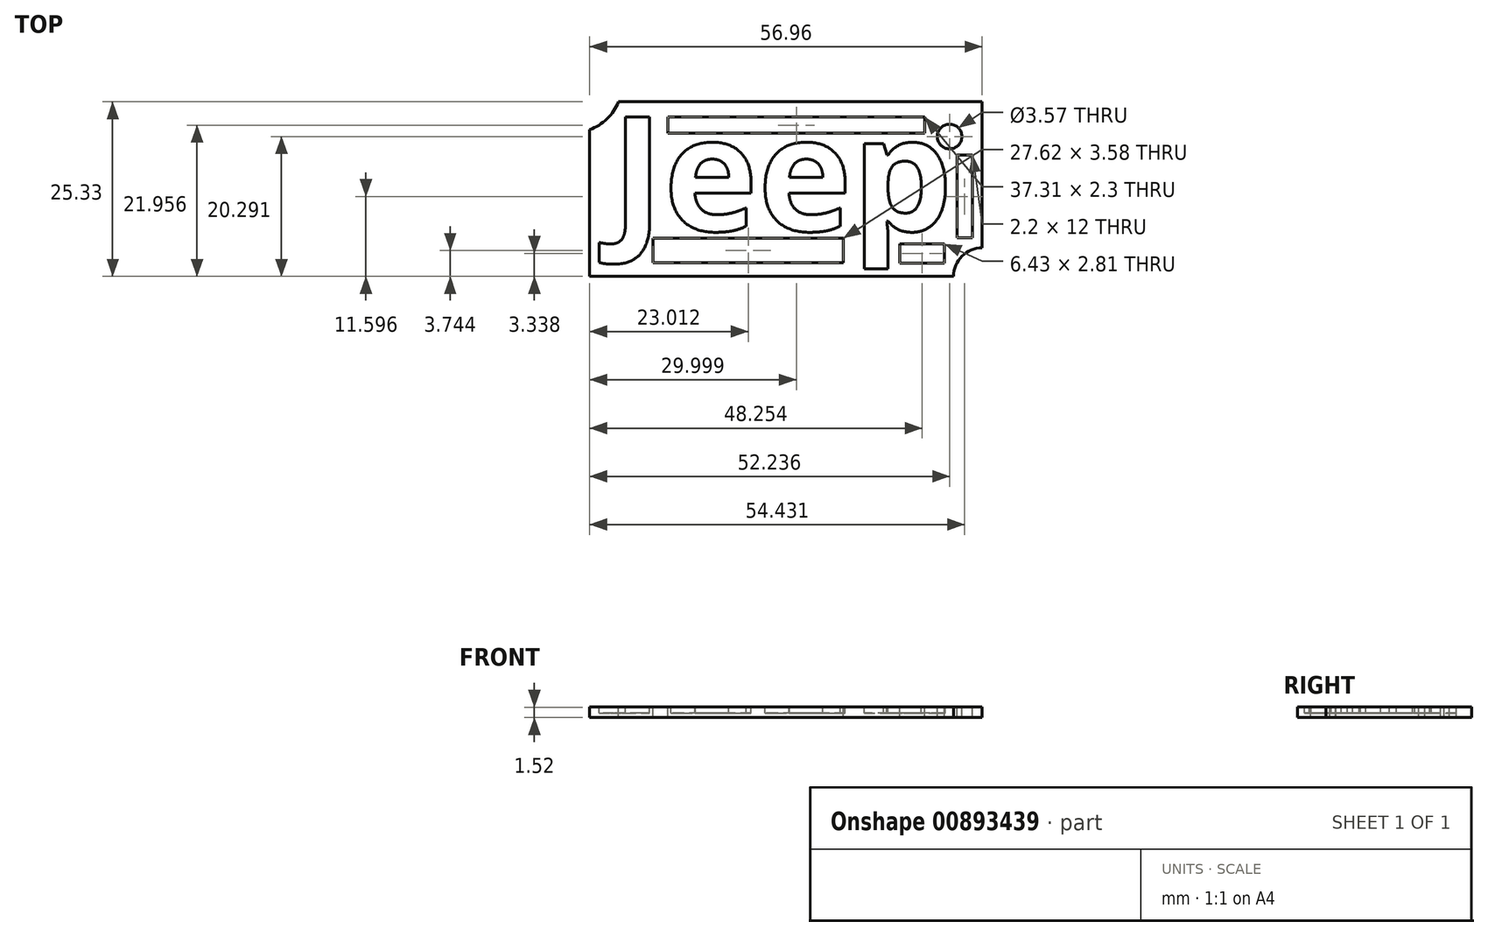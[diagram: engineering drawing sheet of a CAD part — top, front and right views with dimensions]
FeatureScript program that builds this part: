
annotation { "Feature Type Name" : "Feature", "Feature Type Description" : "" }
export const myFeature = defineFeature(function(context is Context, id is Id, definition is map)
    precondition{}
    {
        {
            var Q0;
            Q0=qCreatedBy(makeId("Top.planeOp"),FACE);
            var sketch = newSketch(context, id + "F0", { "sketchPlane" : qUnion([Q0])});
            skLineSegment(sketch, "E0.bottom", {"start": v(-68.58, 25.33) * mm, "end": v(0, 25.33) * mm});
            skLineSegment(sketch, "E0.top", {"start": v(-68.58, 0) * mm, "end": v(0, 0) * mm});
            skLineSegment(sketch, "E0.left", {"start": v(-68.58, 25.33) * mm, "end": v(-68.58, 0) * mm});
            skLineSegment(sketch, "E0.right", {"start": v(0, 25.33) * mm, "end": v(0, 0) * mm});
            skSolve(sketch);
        }
        {
            var Q0;
            Q0 = qSketchRegion(id + "F0", true);
            extrude(context, id + "F1", {"entities" : qUnion([Q0]), "depth" : 1.52 * mm, "offsetDistance" : 25.4 * mm});
        }
        {
            var Q0;
            Q0=makeQuery(id+"F1.opExtrude","CAP_FACE",FACE,{"disambiguationData":[OSD([sQuery(id+"F0.wireOp",EDGE,"E0.bottom"),sQuery(id+"F0.wireOp",EDGE,"E0.top"),sQuery(id+"F0.wireOp",EDGE,"E0.left"),sQuery(id+"F0.wireOp",EDGE,"E0.right")])],"isStart":false});
            var sketch = newSketch(context, id + "F2", { "sketchPlane" : qUnion([Q0])});
            skText(sketch, "E1", { "text": "Jeep", "fontName": "OpenSans-Bold.ttf"});
            const initialGuessF2  = {"E1": [-0.06546, 0.00662, 1, 0, 0.01663]};
            skSetInitialGuess(sketch, initialGuessF2);
            skSolve(sketch);
        }
        {
            var Q0;
            Q0 = qSketchRegion(id + "F2", true);
            extrude(context, id + "F3", {"entities" : qUnion([Q0]), "operationType" : NewBodyOperationType.REMOVE, "oppositeDirection" : true, "depth" : 0.86 * mm, "offsetDistance" : 25.4 * mm});
        }
        {
            var Q0;
            {var subQ0=sQuery(id+"F0.wireOp",EDGE,"E0.left");var subQ1=sQuery(id+"F0.wireOp",EDGE,"E0.bottom");var subQ2=sQuery(id+"F0.wireOp",EDGE,"E0.right");var subQ3=sQuery(id+"F0.wireOp",EDGE,"E0.top");Q0=makeQuery(id+"F3.boolean.opBoolean","SPLIT",FACE,{"disambiguationData":[TD([makeQuery(id+"F1.opExtrude","SWEPT_FACE",FACE,{"disambiguationData":[OSD([subQ1])]})])],"derivedFrom":makeQuery(id+"F1.opExtrude","CAP_FACE",FACE,{"disambiguationData":[OSD([subQ1,subQ3,subQ0,subQ2])],"isStart":false})});}
            var sketch = newSketch(context, id + "F4", { "sketchPlane" : qUnion([Q0])});
            skLineSegment(sketch, "E2.bottom", {"start": v(-11.62, 32.09) * mm, "end": v(9.77, 32.09) * mm});
            skLineSegment(sketch, "E2.top", {"start": v(-11.62, -12.1) * mm, "end": v(9.77, -12.1) * mm});
            skLineSegment(sketch, "E2.left", {"start": v(-11.62, 32.09) * mm, "end": v(-11.62, -12.1) * mm});
            skLineSegment(sketch, "E2.right", {"start": v(9.77, 32.09) * mm, "end": v(9.77, -12.1) * mm});
            skSolve(sketch);
        }
        {
            var Q0;
            Q0 = qSketchRegion(id + "F4", true);
            extrude(context, id + "F5", {"entities" : qUnion([Q0]), "operationType" : NewBodyOperationType.REMOVE, "oppositeDirection" : true, "depth" : 64 * mm, "offsetDistance" : 25.4 * mm});
        }
        {
            var Q0;
            {var subQ0=sQuery(id+"F0.wireOp",EDGE,"E0.left");var subQ1=sQuery(id+"F0.wireOp",EDGE,"E0.bottom");var subQ2=sQuery(id+"F0.wireOp",EDGE,"E0.right");var subQ3=sQuery(id+"F0.wireOp",EDGE,"E0.top");Q0=makeQuery(id+"F3.boolean.opBoolean","SPLIT",FACE,{"disambiguationData":[TD([makeQuery(id+"F1.opExtrude","SWEPT_FACE",FACE,{"disambiguationData":[OSD([subQ1])]})])],"derivedFrom":makeQuery(id+"F1.opExtrude","CAP_FACE",FACE,{"disambiguationData":[OSD([subQ1,subQ3,subQ0,subQ2])],"isStart":false})});}
            var sketch = newSketch(context, id + "F6", { "sketchPlane" : qUnion([Q0])});
            skCircle(sketch, "E3", {"center": v(-16.34, 20.3) * mm, "radius": 1.78 * mm});
            skSolve(sketch);
        }
        {
            var Q0;
            Q0 = qSketchRegion(id + "F6", true);
            extrude(context, id + "F7", {"entities" : qUnion([Q0]), "operationType" : NewBodyOperationType.REMOVE, "oppositeDirection" : true, "depth" : 17.58 * mm, "offsetDistance" : 25.4 * mm});
        }
        {
            var Q0;
            {var subQ0=sQuery(id+"F0.wireOp",EDGE,"E0.left");var subQ1=sQuery(id+"F0.wireOp",EDGE,"E0.bottom");var subQ2=sQuery(id+"F0.wireOp",EDGE,"E0.right");var subQ3=sQuery(id+"F0.wireOp",EDGE,"E0.top");Q0=makeQuery(id+"F3.boolean.opBoolean","SPLIT",FACE,{"disambiguationData":[TD([makeQuery(id+"F1.opExtrude","SWEPT_FACE",FACE,{"disambiguationData":[OSD([subQ1])]})])],"derivedFrom":makeQuery(id+"F1.opExtrude","CAP_FACE",FACE,{"disambiguationData":[OSD([subQ1,subQ3,subQ0,subQ2])],"isStart":false})});}
            var sketch = newSketch(context, id + "F8", { "sketchPlane" : qUnion([Q0])});
            skCircle(sketch, "E4", {"center": v(-71, 28.01) * mm, "radius": 7.14 * mm});
            skSolve(sketch);
        }
        {
            var Q0;
            Q0 = qSketchRegion(id + "F8", true);
            extrude(context, id + "F9", {"entities" : qUnion([Q0]), "operationType" : NewBodyOperationType.REMOVE, "oppositeDirection" : true, "depth" : 58.67 * mm, "offsetDistance" : 25.4 * mm});
        }
        {
            var Q0;
            {var subQ0=sQuery(id+"F0.wireOp",EDGE,"E0.left");var subQ1=sQuery(id+"F0.wireOp",EDGE,"E0.bottom");var subQ2=sQuery(id+"F0.wireOp",EDGE,"E0.right");var subQ3=sQuery(id+"F0.wireOp",EDGE,"E0.top");Q0=makeQuery(id+"F3.boolean.opBoolean","SPLIT",FACE,{"disambiguationData":[TD([makeQuery(id+"F1.opExtrude","SWEPT_FACE",FACE,{"disambiguationData":[OSD([subQ1])]})])],"derivedFrom":makeQuery(id+"F1.opExtrude","CAP_FACE",FACE,{"disambiguationData":[OSD([subQ1,subQ3,subQ0,subQ2])],"isStart":false})});}
            var sketch = newSketch(context, id + "F10", { "sketchPlane" : qUnion([Q0])});
            skCircle(sketch, "E5", {"center": v(-11.62, 0) * mm, "radius": 4.16 * mm});
            skSolve(sketch);
        }
        {
            var Q0;
            Q0 = qSketchRegion(id + "F10", true);
            extrude(context, id + "F11", {"entities" : qUnion([Q0]), "operationType" : NewBodyOperationType.REMOVE, "oppositeDirection" : true, "depth" : 87.88 * mm, "offsetDistance" : 25.4 * mm});
        }
        {
            var Q0;
            {var subQ0=sQuery(id+"F0.wireOp",EDGE,"E0.left");var subQ1=sQuery(id+"F0.wireOp",EDGE,"E0.bottom");var subQ2=sQuery(id+"F0.wireOp",EDGE,"E0.right");var subQ3=sQuery(id+"F0.wireOp",EDGE,"E0.top");Q0=makeQuery(id+"F3.boolean.opBoolean","SPLIT",FACE,{"disambiguationData":[TD([makeQuery(id+"F1.opExtrude","SWEPT_FACE",FACE,{"disambiguationData":[OSD([subQ1])]})])],"derivedFrom":makeQuery(id+"F1.opExtrude","CAP_FACE",FACE,{"disambiguationData":[OSD([subQ1,subQ3,subQ0,subQ2])],"isStart":false})});}
            var sketch = newSketch(context, id + "F12", { "sketchPlane" : qUnion([Q0])});
            skLineSegment(sketch, "E6.bottom", {"start": v(-59.38, 1.96) * mm, "end": v(-31.76, 1.96) * mm});
            skLineSegment(sketch, "E6.top", {"start": v(-59.38, 5.53) * mm, "end": v(-31.76, 5.53) * mm});
            skLineSegment(sketch, "E6.left", {"start": v(-59.38, 1.96) * mm, "end": v(-59.38, 5.53) * mm});
            skLineSegment(sketch, "E6.right", {"start": v(-31.76, 1.96) * mm, "end": v(-31.76, 5.53) * mm});
            skSolve(sketch);
        }
        {
            var Q0;
            Q0 = qSketchRegion(id + "F12", true);
            extrude(context, id + "F13", {"entities" : qUnion([Q0]), "operationType" : NewBodyOperationType.REMOVE, "oppositeDirection" : true, "depth" : 5.08 * mm, "offsetDistance" : 25.4 * mm});
        }
        {
            var Q0;
            {var subQ0=sQuery(id+"F0.wireOp",EDGE,"E0.left");var subQ1=sQuery(id+"F0.wireOp",EDGE,"E0.bottom");var subQ2=sQuery(id+"F0.wireOp",EDGE,"E0.right");var subQ3=sQuery(id+"F0.wireOp",EDGE,"E0.top");Q0=makeQuery(id+"F3.boolean.opBoolean","SPLIT",FACE,{"disambiguationData":[TD([makeQuery(id+"F1.opExtrude","SWEPT_FACE",FACE,{"disambiguationData":[OSD([subQ1])]})])],"derivedFrom":makeQuery(id+"F1.opExtrude","CAP_FACE",FACE,{"disambiguationData":[OSD([subQ1,subQ3,subQ0,subQ2])],"isStart":false})});}
            var sketch = newSketch(context, id + "F14", { "sketchPlane" : qUnion([Q0])});
            skLineSegment(sketch, "E7.bottom", {"start": v(-57.23, 23.1) * mm, "end": v(-19.93, 23.1) * mm});
            skLineSegment(sketch, "E7.top", {"start": v(-57.23, 20.8) * mm, "end": v(-19.93, 20.8) * mm});
            skLineSegment(sketch, "E7.left", {"start": v(-57.23, 23.1) * mm, "end": v(-57.23, 20.8) * mm});
            skLineSegment(sketch, "E7.right", {"start": v(-19.93, 23.1) * mm, "end": v(-19.93, 20.8) * mm});
            skSolve(sketch);
        }
        {
            var Q0;
            Q0 = qSketchRegion(id + "F14", true);
            extrude(context, id + "F15", {"entities" : qUnion([Q0]), "operationType" : NewBodyOperationType.REMOVE, "oppositeDirection" : true, "depth" : 22.6 * mm, "offsetDistance" : 25.4 * mm});
        }
        {
            var Q0;
            {var subQ0=sQuery(id+"F0.wireOp",EDGE,"E0.left");var subQ1=sQuery(id+"F0.wireOp",EDGE,"E0.bottom");var subQ2=sQuery(id+"F0.wireOp",EDGE,"E0.right");var subQ3=sQuery(id+"F0.wireOp",EDGE,"E0.top");Q0=makeQuery(id+"F3.boolean.opBoolean","SPLIT",FACE,{"disambiguationData":[TD([makeQuery(id+"F1.opExtrude","SWEPT_FACE",FACE,{"disambiguationData":[OSD([subQ1])]})])],"derivedFrom":makeQuery(id+"F1.opExtrude","CAP_FACE",FACE,{"disambiguationData":[OSD([subQ1,subQ3,subQ0,subQ2])],"isStart":false})});}
            var sketch = newSketch(context, id + "F16", { "sketchPlane" : qUnion([Q0])});
            skLineSegment(sketch, "E8.bottom", {"start": v(-15.25, 17.6) * mm, "end": v(-13.05, 17.6) * mm});
            skLineSegment(sketch, "E8.top", {"start": v(-15.25, 5.6) * mm, "end": v(-13.05, 5.6) * mm});
            skLineSegment(sketch, "E8.left", {"start": v(-15.25, 17.6) * mm, "end": v(-15.25, 5.6) * mm});
            skLineSegment(sketch, "E8.right", {"start": v(-13.05, 17.6) * mm, "end": v(-13.05, 5.6) * mm});
            skSolve(sketch);
        }
        {
            var Q0;
            Q0 = qSketchRegion(id + "F16", true);
            extrude(context, id + "F17", {"entities" : qUnion([Q0]), "operationType" : NewBodyOperationType.REMOVE, "oppositeDirection" : true, "depth" : 13.46 * mm, "offsetDistance" : 25.4 * mm});
        }
        {
            var Q0;
            {var subQ0=sQuery(id+"F0.wireOp",EDGE,"E0.left");var subQ1=sQuery(id+"F0.wireOp",EDGE,"E0.bottom");var subQ2=sQuery(id+"F0.wireOp",EDGE,"E0.right");var subQ3=sQuery(id+"F0.wireOp",EDGE,"E0.top");Q0=makeQuery(id+"F3.boolean.opBoolean","SPLIT",FACE,{"disambiguationData":[TD([makeQuery(id+"F1.opExtrude","SWEPT_FACE",FACE,{"disambiguationData":[OSD([subQ1])]})])],"derivedFrom":makeQuery(id+"F1.opExtrude","CAP_FACE",FACE,{"disambiguationData":[OSD([subQ1,subQ3,subQ0,subQ2])],"isStart":false})});}
            var sketch = newSketch(context, id + "F18", { "sketchPlane" : qUnion([Q0])});
            skLineSegment(sketch, "E9.bottom", {"start": v(-23.54, 4.74) * mm, "end": v(-17.1, 4.74) * mm});
            skLineSegment(sketch, "E9.top", {"start": v(-23.54, 1.93) * mm, "end": v(-17.1, 1.93) * mm});
            skLineSegment(sketch, "E9.left", {"start": v(-23.54, 4.74) * mm, "end": v(-23.54, 1.93) * mm});
            skLineSegment(sketch, "E9.right", {"start": v(-17.1, 4.74) * mm, "end": v(-17.1, 1.93) * mm});
            skSolve(sketch);
        }
        {
            var Q0;
            Q0=makeQuery(id+"F18.imprint","IMPRINT",FACE,{"disambiguationData":[TD([[makeQuery(id+"F18.imprint","IMPRINT",EDGE,{"derivedFrom":sQuery(id+"F18.wireOp",EDGE,"E9.bottom")}),-1.0]])]});
            extrude(context, id + "F19", {"entities" : qUnion([Q0]), "operationType" : NewBodyOperationType.REMOVE, "oppositeDirection" : true, "depth" : 16.26 * mm, "offsetDistance" : 25.4 * mm});
        }
    });
